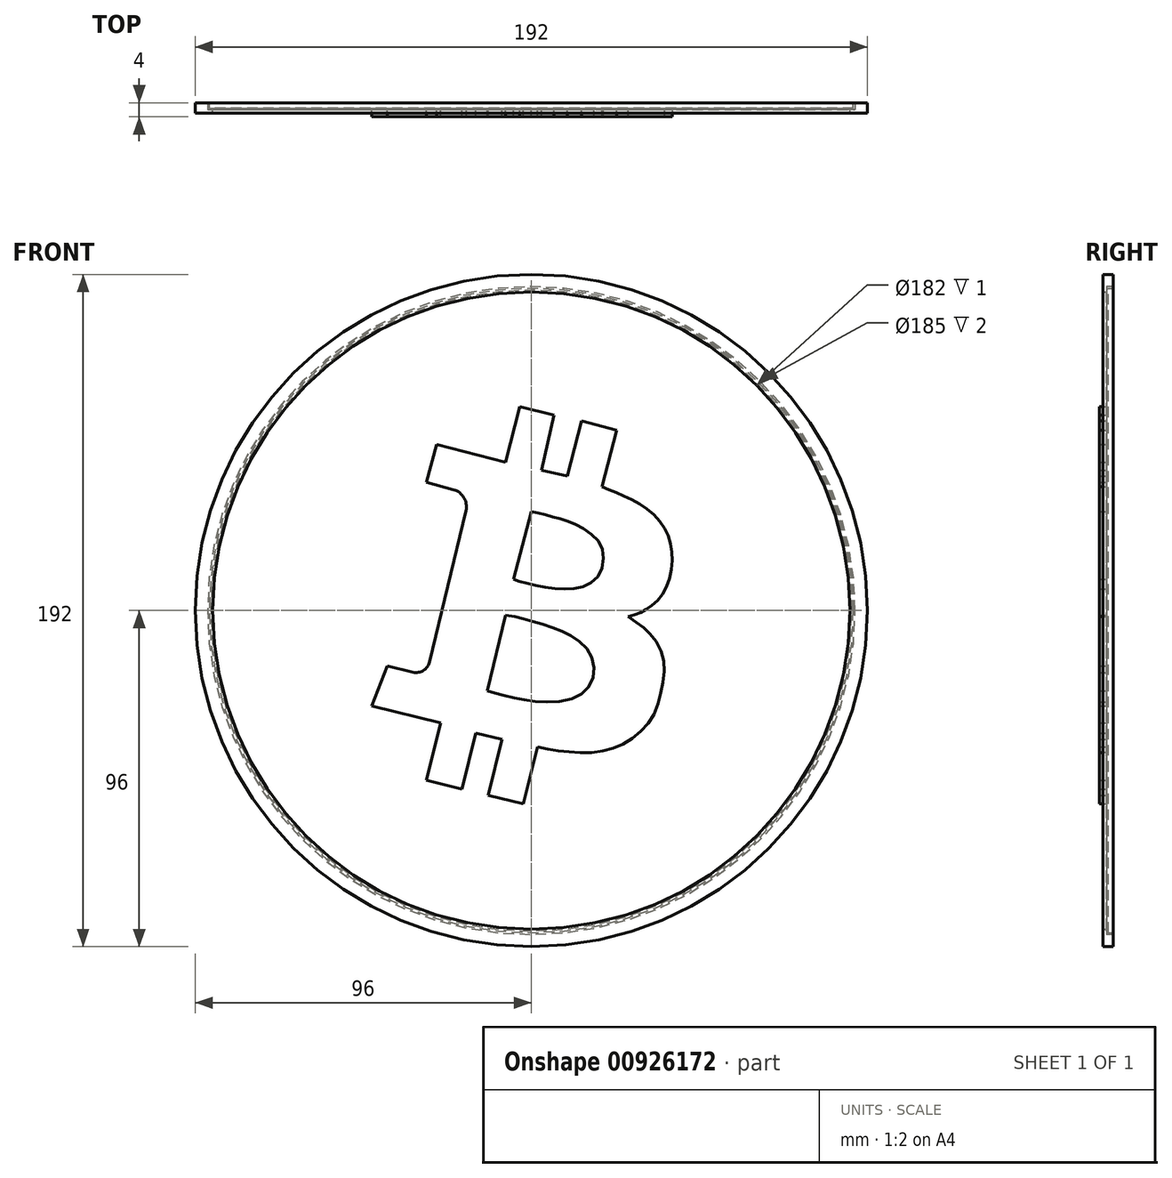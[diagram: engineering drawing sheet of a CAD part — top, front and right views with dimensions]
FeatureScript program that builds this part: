
annotation { "Feature Type Name" : "Feature", "Feature Type Description" : "" }
export const myFeature = defineFeature(function(context is Context, id is Id, definition is map)
    precondition{}
    {
        {
            var Q0;
            Q0=qCreatedBy(makeId("Front.planeOp"),FACE);
            var sketch = newSketch(context, id + "F0", { "sketchPlane" : qUnion([Q0])});
            skCircle(sketch, "E0", {"center": v(0, 0) * mm, "radius": 92 * mm});
            skSolve(sketch);
        }
        {
            var Q0;
            Q0 = qSketchRegion(id + "F0", true);
            extrude(context, id + "F1", {"entities" : qUnion([Q0]), "depth" : 2 * mm, "offsetDistance" : 25 * mm});
        }
        {
            var Q0;
            Q0=makeQuery(id+"F1.opExtrude","CAP_FACE",FACE,{"disambiguationData":[OSD([sQuery(id+"F0.wireOp",EDGE,"E0")])],"isStart":false});
            var sketch = newSketch(context, id + "F2", { "sketchPlane" : qUnion([Q0])});
            skPoint(sketch, "E1", {"position": v(0, 92) * mm});
            skPoint(sketch, "E2", {"position": v(-92, 0) * mm});
            skLineSegment(sketch, "E3", {"start": v(-29.98, 36.66) * mm, "end": v(-27, 47.45) * mm});
            skLineSegment(sketch, "E4", {"start": v(-27, 47.45) * mm, "end": v(-7.4, 42.4) * mm});
            skLineSegment(sketch, "E5", {"start": v(-7.4, 42.4) * mm, "end": v(-3.3, 58.28) * mm});
            skLineSegment(sketch, "E6", {"start": v(-3.3, 58.28) * mm, "end": v(6.51, 55.75) * mm});
            skLineSegment(sketch, "E7", {"start": v(6.51, 55.75) * mm, "end": v(2.9, 40.11) * mm});
            skLineSegment(sketch, "E8", {"start": v(2.9, 40.11) * mm, "end": v(10.32, 38.4) * mm});
            skLineSegment(sketch, "E9", {"start": v(10.32, 38.4) * mm, "end": v(14.35, 54.1) * mm});
            skLineSegment(sketch, "E10", {"start": v(14.35, 54.1) * mm, "end": v(24.32, 51.55) * mm});
            skLineSegment(sketch, "E11", {"start": v(24.32, 51.55) * mm, "end": v(20.17, 35.4) * mm});
            skLineSegment(sketch, "E12", {"start": v(-29.98, 36.66) * mm, "end": v(-22.23, 34.53) * mm});
            skLineSegment(sketch, "E13", {"start": v(-18.7, 28.54) * mm, "end": v(-29.04, -14.63) * mm});
            skLineSegment(sketch, "E14", {"start": v(-33.87, -17.6) * mm, "end": v(-41.09, -15.86) * mm});
            skLineSegment(sketch, "E15", {"start": v(-41.09, -15.86) * mm, "end": v(-45.58, -27.2) * mm});
            skLineSegment(sketch, "E16", {"start": v(-45.58, -27.2) * mm, "end": v(-25.96, -32.13) * mm});
            skLineSegment(sketch, "E17", {"start": v(-25.96, -32.13) * mm, "end": v(-29.98, -48.44) * mm});
            skLineSegment(sketch, "E18", {"start": v(-29.98, -48.44) * mm, "end": v(-19.82, -50.94) * mm});
            skLineSegment(sketch, "E19", {"start": v(-19.82, -50.94) * mm, "end": v(-15.88, -34.94) * mm});
            skLineSegment(sketch, "E20", {"start": v(-15.88, -34.94) * mm, "end": v(-8.42, -36.77) * mm});
            skLineSegment(sketch, "E21", {"start": v(-8.42, -36.77) * mm, "end": v(-12.35, -52.73) * mm});
            skLineSegment(sketch, "E22", {"start": v(-12.35, -52.73) * mm, "end": v(-2.28, -55.2) * mm});
            skLineSegment(sketch, "E23", {"start": v(-2.28, -55.2) * mm, "end": v(1.73, -38.9) * mm});
            skLineSegment(sketch, "E24", {"start": v(-12.58, -22.87) * mm, "end": v(-7.4, -1.28) * mm});
            skLineSegment(sketch, "E25", {"start": v(-5.13, 8.93) * mm, "end": v(0, 28.28) * mm});
            skFitSpline(sketch, "E26", {"points": [v(20.17, 35.4) * mm, v(24.32, 33.63) * mm, v(29.21, 31.36) * mm, v(34.2, 28.13) * mm, v(37.87, 23.84) * mm, v(39.7, 19.2) * mm, v(40.23, 13.79) * mm, v(39.1, 7.93) * mm, v(36.46, 3.3) * mm, v(33.4, 0.76) * mm, v(30.78, -0.73) * mm, v(27.63, -1.77) * mm], "startDerivative": vector(49.6, -23.88) * mm, "endDerivative": vector(-43.55, -12.55) * mm});
            skFitSpline(sketch, "E27", {"points": [v(27.63, -1.77) * mm, v(30.75, -3.88) * mm, v(33.1, -5.8) * mm, v(35.38, -8.43) * mm, v(37.4, -12.45) * mm, v(38, -16.3) * mm, v(37.5, -21.07) * mm, v(36.51, -25.53) * mm, v(34.78, -30.1) * mm, v(32.18, -33.56) * mm, v(28.6, -36.65) * mm, v(24.51, -38.88) * mm, v(20.43, -40.12) * mm, v(15.48, -40.61) * mm, v(10.53, -40.36) * mm, v(6.08, -39.87) * mm, v(1.73, -38.9) * mm], "startDerivative": vector(55.75, -36.46) * mm, "endDerivative": vector(-68.53, 17.03) * mm});
            skFitSpline(sketch, "E28", {"points": [v(0, 28.28) * mm, v(2.03, 27.84) * mm, v(4.43, 27.27) * mm, v(6.62, 26.62) * mm, v(9.38, 25.83) * mm, v(12.09, 24.78) * mm, v(14.8, 23.52) * mm, v(18, 21.06) * mm, v(20.17, 18.03) * mm, v(20.6, 14.5) * mm, v(19.6, 10.55) * mm, v(17.07, 7.96) * mm, v(14.16, 6.66) * mm, v(10.4, 6.16) * mm, v(6.43, 6.35) * mm, v(2.54, 6.97) * mm, v(-0.99, 7.7) * mm, v(-3.53, 8.39) * mm, v(-5.13, 8.93) * mm], "startDerivative": vector(43.85, -7.74) * mm, "endDerivative": vector(-35.64, 18.42) * mm});
            skPoint(sketch, "E29.visualSharp", {"position": v(-29.98, -18.52) * mm});
            skArc(sketch, "E29.filletArc", {"start": v(-33.87, -17.6) * mm, "mid": v(-30.84, -17.11) * mm, "end": v(-29.04, -14.63) * mm});
            skPoint(sketch, "E30.visualSharp", {"position": v(-17.56, 33.24) * mm});
            skArc(sketch, "E30.filletArc", {"start": v(-18.7, 28.54) * mm, "mid": v(-19.25, 32.25) * mm, "end": v(-22.23, 34.53) * mm});
            skFitSpline(sketch, "E31", {"points": [v(-7.4, -1.28) * mm, v(-4.7, -1.77) * mm, v(-2.56, -2.3) * mm, v(0, -2.97) * mm, v(3, -3.83) * mm, v(5.97, -4.83) * mm, v(8.94, -5.97) * mm, v(11.43, -7.28) * mm, v(13.9, -8.95) * mm, v(16.07, -11.17) * mm, v(17.42, -13.92) * mm, v(17.9, -16.98) * mm, v(17.42, -19.83) * mm, v(15.84, -22.45) * mm, v(13.44, -24.33) * mm, v(9.5, -25.73) * mm, v(4.9, -26.12) * mm, v(1.02, -25.9) * mm, v(-2.66, -25.38) * mm, v(-5.68, -24.72) * mm, v(-9.13, -23.9) * mm, v(-10.66, -23.5) * mm, v(-12.58, -22.87) * mm], "startDerivative": vector(56.77, -8.84) * mm, "endDerivative": vector(-54.89, 18.56) * mm});
            skSolve(sketch);
        }
        {
            var Q0;
            Q0 = qSketchRegion(id + "F2", true);
            extrude(context, id + "F3", {"entities" : qUnion([Q0]), "operationType" : NewBodyOperationType.ADD, "depth" : 2 * mm, "offsetDistance" : 25 * mm});
        }
        {
            var Q0;
            Q0=makeQuery(id+"F1.opExtrude","CAP_EDGE",EDGE,{"disambiguationData":[OSD([sQuery(id+"F0.wireOp",EDGE,"E0")])],"isStart":false});
            chamfer(context, id + "F4", {"entities" : qUnion([Q0]), "width" : 0.5 * mm, "tangentPropagation" : true});
        }
        {
            var Q0;
            {var subQ0=sQuery(id+"F0.wireOp",EDGE,"E0");Q0=makeQuery(id+"F3.boolean.opBoolean","SPLIT",FACE,{"disambiguationData":[TD([makeQuery(id+"F1.opExtrude","SWEPT_FACE",FACE,{"disambiguationData":[OSD([subQ0])]})])],"derivedFrom":makeQuery(id+"F1.opExtrude","CAP_FACE",FACE,{"disambiguationData":[OSD([subQ0])],"isStart":false})});}
            var sketch = newSketch(context, id + "F5", { "sketchPlane" : qUnion([Q0])});
            skCircle(sketch, "E32", {"center": v(0, 0) * mm, "radius": 91 * mm});
            skCircle(sketch, "E33", {"center": v(0, 0) * mm, "radius": 96 * mm});
            skSolve(sketch);
        }
        {
            var Q0;
            Q0 = qSketchRegion(id + "F5", true);
            extrude(context, id + "F6", {"entities" : qUnion([Q0]), "depth" : 1 * mm, "offsetDistance" : 25 * mm});
        }
        {
            var Q0;
            Q0=makeQuery(id+"F6.opExtrude","CAP_FACE",FACE,{"disambiguationData":[OSD([sQuery(id+"F5.wireOp",EDGE,"E32"),sQuery(id+"F5.wireOp",EDGE,"E33")])],"isStart":true});
            var sketch = newSketch(context, id + "F7", { "sketchPlane" : qUnion([Q0])});
            skCircle(sketch, "E34", {"center": v(0, 0) * mm, "radius": 96 * mm});
            skCircle(sketch, "E35", {"center": v(0, 0) * mm, "radius": 92.5 * mm});
            skSolve(sketch);
        }
        {
            var Q0;
            Q0 = qSketchRegion(id + "F7", true);
            extrude(context, id + "F8", {"entities" : qUnion([Q0]), "operationType" : NewBodyOperationType.ADD, "depth" : 2 * mm, "offsetDistance" : 25 * mm});
        }
    });
